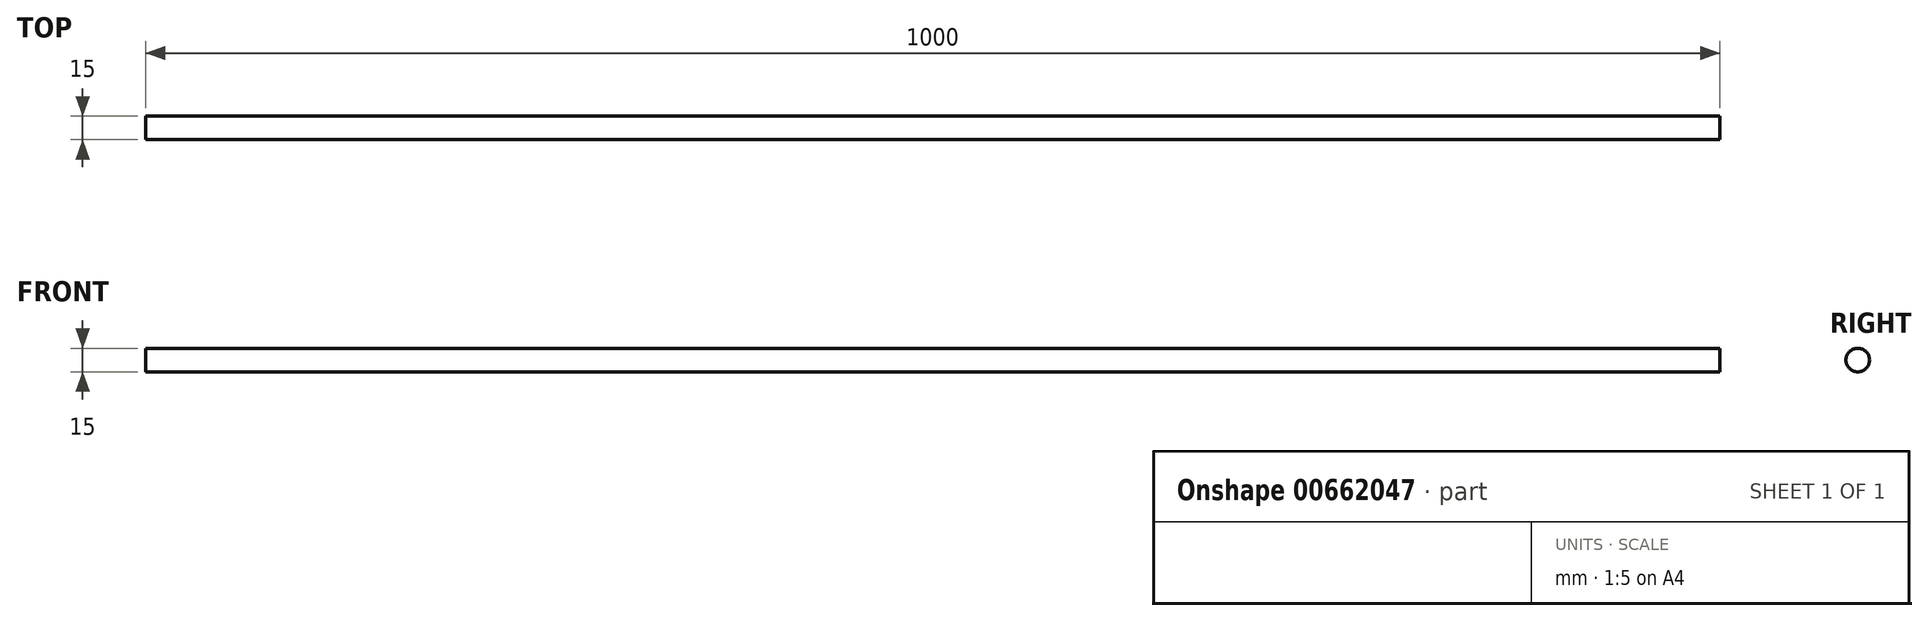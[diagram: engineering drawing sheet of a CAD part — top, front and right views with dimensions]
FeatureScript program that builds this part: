
annotation { "Feature Type Name" : "Feature", "Feature Type Description" : "" }
export const myFeature = defineFeature(function(context is Context, id is Id, definition is map)
    precondition{}
    {
        {
            var Q0;
            Q0=qCreatedBy(makeId("Front.planeOp"),FACE);
            var sketch = newSketch(context, id + "F0", { "sketchPlane" : qUnion([Q0])});
            skLineSegment(sketch, "E0.bottom", {"start": v(-94.74, 7.5) * mm, "end": v(905.26, 7.5) * mm});
            skLineSegment(sketch, "E0.top", {"start": v(-94.74, 0) * mm, "end": v(905.26, 0) * mm});
            skLineSegment(sketch, "E0.left", {"start": v(-94.74, 7.5) * mm, "end": v(-94.74, 0) * mm});
            skLineSegment(sketch, "E0.right", {"start": v(905.26, 7.5) * mm, "end": v(905.26, 0) * mm});
            skSolve(sketch);
        }
        {
            var Q0;
            Q0=makeQuery(id+"F0.imprint","IMPRINT",FACE,{"disambiguationData":[TD([[makeQuery(id+"F0.imprint","IMPRINT",EDGE,{"derivedFrom":sQuery(id+"F0.wireOp",EDGE,"E0.bottom")}),-1.0]])]});
            var Q1;
            Q1=sQuery(id+"F0.wireOp",EDGE,"E0.top");
            revolve(context, id + "F1", {"entities" : qUnion([Q0]), "axis" : qUnion([Q1]), "revolveType" : RevolveType.FULL});
        }
    });
